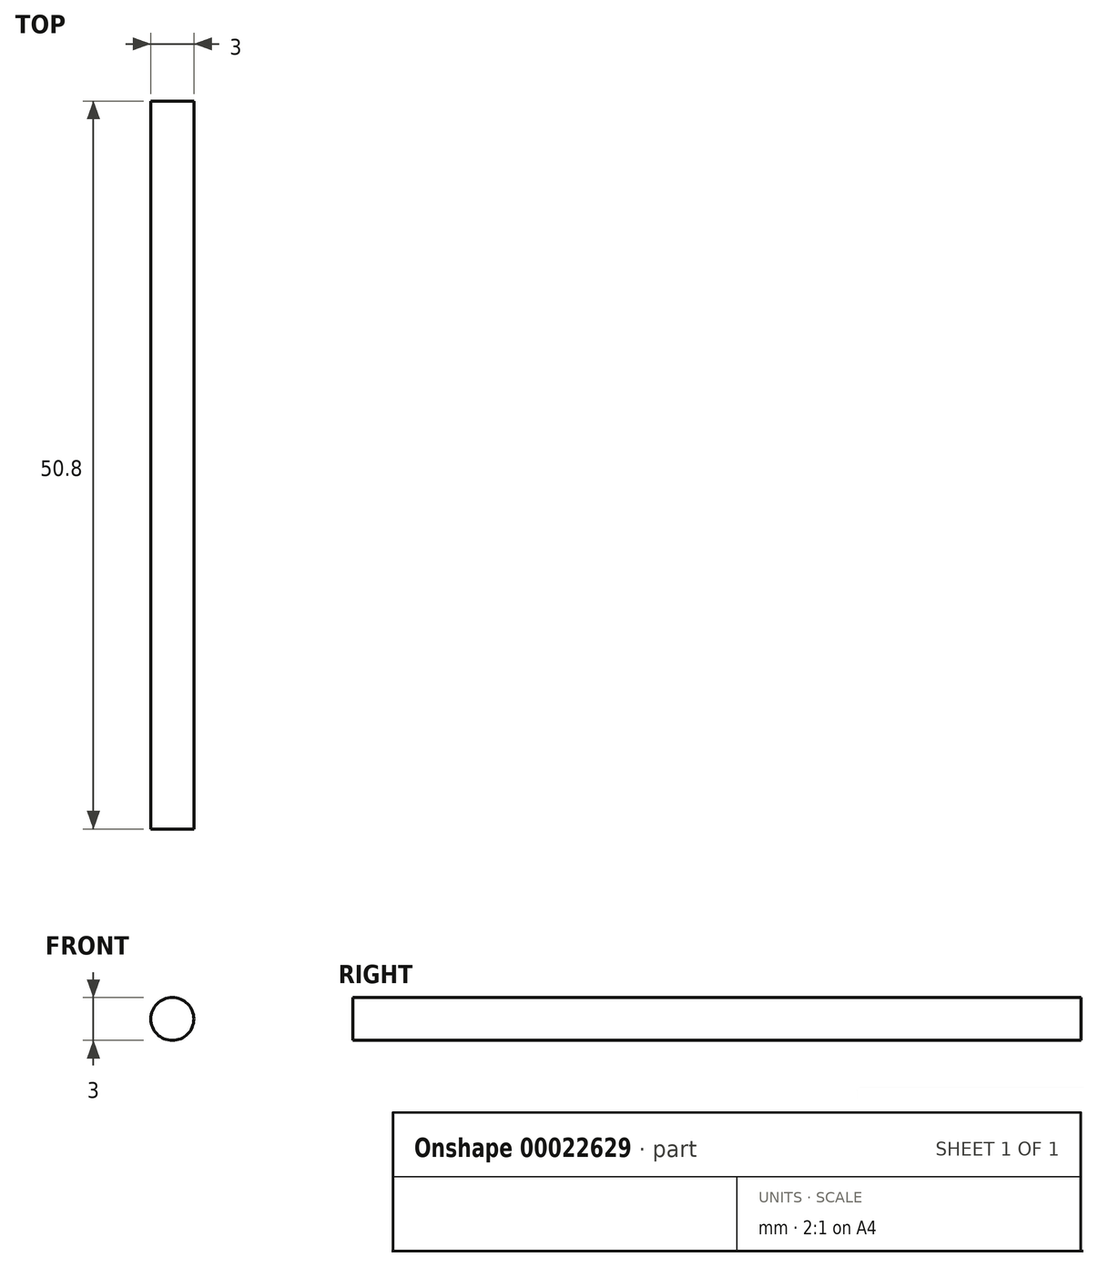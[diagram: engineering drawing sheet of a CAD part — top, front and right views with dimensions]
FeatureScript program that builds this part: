
annotation { "Feature Type Name" : "Feature", "Feature Type Description" : "" }
export const myFeature = defineFeature(function(context is Context, id is Id, definition is map)
    precondition{}
    {
        {
            var Q0;
            Q0=qCreatedBy(makeId("Front.planeOp"),FACE);
            var sketch = newSketch(context, id + "F0", { "sketchPlane" : qUnion([Q0])});
            skCircle(sketch, "E0", {"center": v(0, 0) * mm, "radius": 1.5 * mm});
            skSolve(sketch);
        }
        {
            var Q0;
            Q0 = qSketchRegion(id + "F0", true);
            extrude(context, id + "F1", {"entities" : qUnion([Q0]), "oppositeDirection" : true, "depth" : 50.8 * mm});
        }
    });
